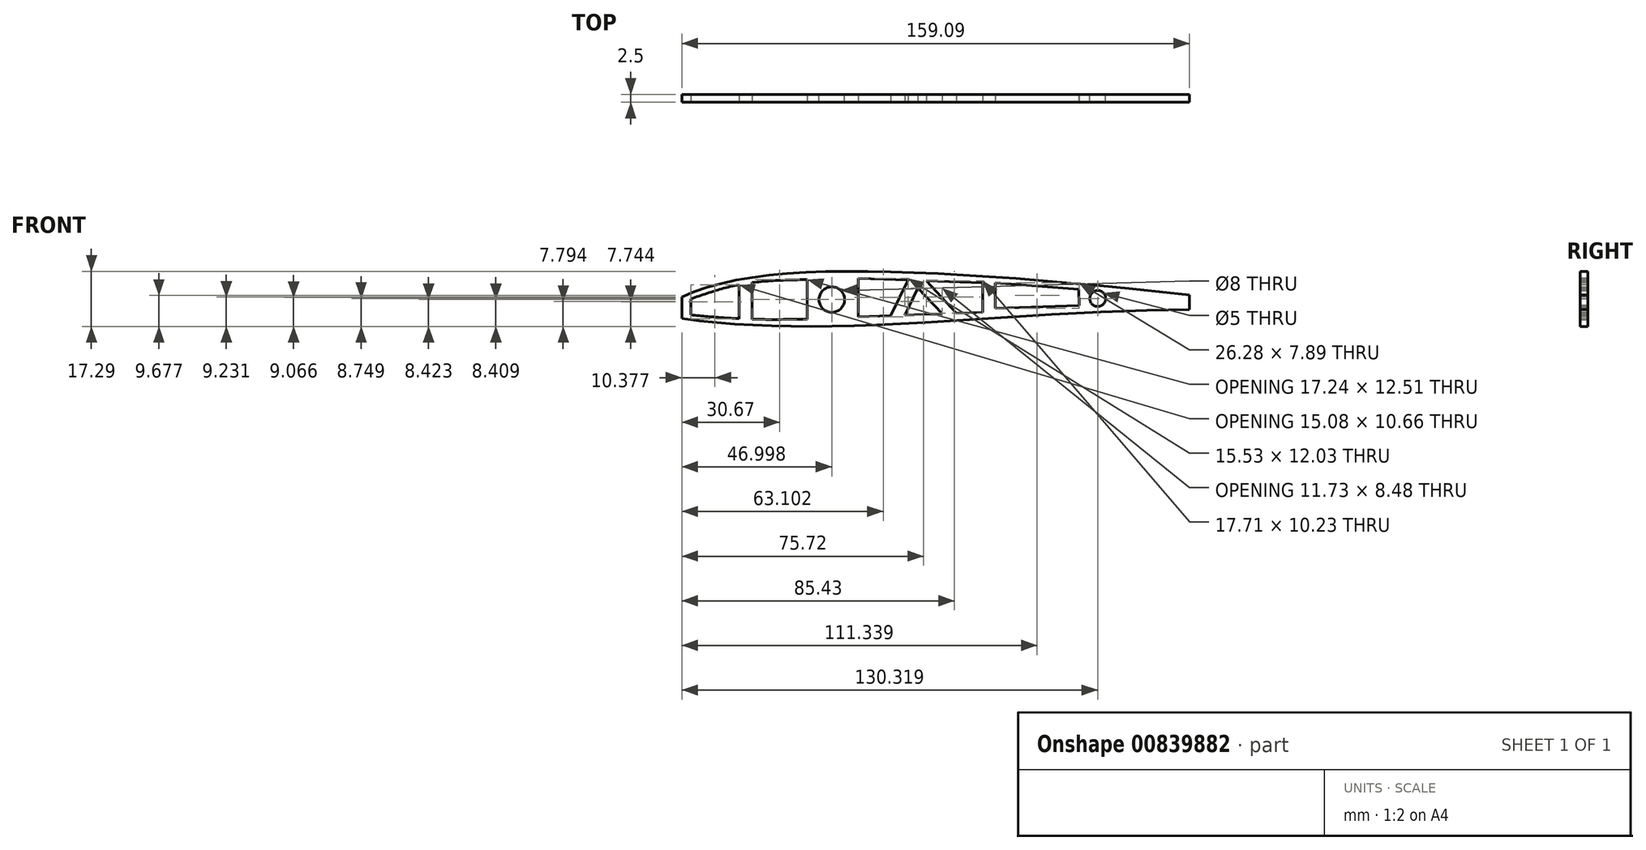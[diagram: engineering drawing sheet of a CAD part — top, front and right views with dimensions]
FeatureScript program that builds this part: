
annotation { "Feature Type Name" : "Feature", "Feature Type Description" : "" }
export const myFeature = defineFeature(function(context is Context, id is Id, definition is map)
    precondition{}
    {
        {
            var Q0;
            Q0=qCreatedBy(makeId("Front.planeOp"),FACE);
            var sketch = newSketch(context, id + "F0", { "sketchPlane" : qUnion([Q0])});
            skPoint(sketch, "E0.middle", {"position": v(0, 0) * mm});
            skLineSegment(sketch, "E1", {"start": v(-99.95, -4.05) * mm, "end": v(-99.64, -4.05) * mm});
            skFitSpline(sketch, "E2", {"points": [v(-96.98, -0.81) * mm, v(-45.24, 7.5) * mm, v(100, -4.05) * mm], "startDerivative": vector(97.58, 47.67) * mm, "endDerivative": vector(275.05, -31.29) * mm});
            skFitSpline(sketch, "E3", {"points": [v(-96.54, -7.34) * mm, v(-44.56, -9.6) * mm, v(41.7, -4.97) * mm, v(100, -4.05) * mm], "startDerivative": vector(159.07, -20.98) * mm, "endDerivative": vector(169.88, 6) * mm});
            skFitSpline(sketch, "E4", {"points": [v(-96.54, -7.34) * mm, v(-101.41, -5) * mm, v(-96.98, -0.81) * mm], "startDerivative": vector(-18.7, 3.9) * mm, "endDerivative": vector(17.62, 9.13) * mm});
            skArc(sketch, "E5.trimOffspring", {"start": v(-97.54, -7.12) * mm, "mid": v(-97.05, -7.27) * mm, "end": v(-96.54, -7.34) * mm});
            skFitSpline(sketch, "E6", {"points": [v(-96.34, -1.64) * mm, v(-45.34, 6.27) * mm, v(86.1, -3.38) * mm], "startDerivative": vector(82.57, 38.4) * mm, "endDerivative": vector(239.73, -24.74) * mm});
            skFitSpline(sketch, "E7", {"points": [v(-97.38, -6.05) * mm, v(-44.49, -7.96) * mm, v(41.39, -3.9) * mm, v(86.1, -3.38) * mm], "startDerivative": vector(144.05, -26.77) * mm, "endDerivative": vector(139.27, -2.3) * mm});
            skFitSpline(sketch, "E8", {"points": [v(-97.38, -6.05) * mm, v(-99.95, -4.56) * mm, v(-96.34, -1.64) * mm], "startDerivative": vector(-8.62, 1.03) * mm, "endDerivative": vector(10.24, 4.38) * mm});
            skSolve(sketch);
        }
        {
            var Q0;
            Q0=qCreatedBy(makeId("Front.planeOp"),FACE);
            var sketch = newSketch(context, id + "F1", { "sketchPlane" : qUnion([Q0])});
            skLineSegment(sketch, "E9", {"start": v(-109.84, -5.04) * mm, "end": v(108.45, -3.99) * mm});
            skCircle(sketch, "E10", {"center": v(-49.54, -1.37) * mm, "radius": 4 * mm});
            skCircle(sketch, "E11", {"center": v(33.78, -1.03) * mm, "radius": 2.5 * mm});
            skSolve(sketch);
        }
        {
            var Q0;
            {var subQ0=sQuery(id+"F0.wireOp",EDGE,"E6");Q0=makeQuery(id+"F0.imprint","IMPRINT",FACE,{"disambiguationData":[TD([[makeQuery(id+"F0.imprint","IMPRINT",EDGE,{"derivedFrom":subQ0}),-1.0]])]});}
            var Q1;
            {var subQ1=sQuery(id+"F0.wireOp",EDGE,"E2");Q1=makeQuery(id+"F0.imprint","IMPRINT",FACE,{"disambiguationData":[TD([[makeQuery(id+"F0.imprint","IMPRINT",EDGE,{"derivedFrom":subQ1}),-1.0]])]});}
            var Q2;
            Q2=makeQuery(id+"F1.imprint","IMPRINT",FACE,{"disambiguationData":[TD([[makeQuery(id+"F1.imprint","IMPRINT",EDGE,{"derivedFrom":sQuery(id+"F1.wireOp",EDGE,"E11")}),1.0]])]});
            var Q3;
            {var subQ0=sQuery(id+"F1.wireOp",EDGE,"E10");var subQ1=sQuery(id+"F1.wireOp",EDGE,"E9");var subQ2=makeQuery(id+"F1.imprint","INTERSECT",VERTEX,{"disambiguationData":[OD(0.0)],"derivedFrom":[subQ1,subQ0]});Q3=makeQuery(id+"F1.imprint","IMPRINT",FACE,{"disambiguationData":[TD([[makeQuery(id+"F1.imprint","IMPRINT",EDGE,{"disambiguationData":[TD([[subQ2,-1.0]])],"derivedFrom":subQ1}),1.0]])]});}
            var Q4;
            {var subQ0=sQuery(id+"F1.wireOp",EDGE,"E10");var subQ1=sQuery(id+"F1.wireOp",EDGE,"E9");var subQ2=makeQuery(id+"F1.imprint","INTERSECT",VERTEX,{"disambiguationData":[OD(0.0)],"derivedFrom":[subQ1,subQ0]});Q4=makeQuery(id+"F1.imprint","IMPRINT",FACE,{"disambiguationData":[TD([[makeQuery(id+"F1.imprint","IMPRINT",EDGE,{"disambiguationData":[TD([[subQ2,-1.0]])],"derivedFrom":subQ1}),-1.0]])]});}
            var Q5;
            {var subQ0=sQuery(id+"F0.wireOp",EDGE,"E5.trimOffspring");Q5=makeQuery(id+"F0.imprint","IMPRINT",FACE,{"disambiguationData":[TD([[makeQuery(id+"F0.imprint","IMPRINT",EDGE,{"derivedFrom":subQ0}),1.0]])]});}
            extrude(context, id + "F2", {"entities" : qUnion([Q0, Q1, Q2, Q3, Q4, Q5]), "depth" : 2.5 * mm, "offsetDistance" : 25 * mm});
        }
        {
            var Q0;
            Q0=qSketchRegion(id+"F1",true);
            var Q1;
            Q1=sQuery(id+"F1.wireOp",EDGE,"E11");
            var Q2;
            Q2=sQuery(id+"F1.wireOp",EDGE,"E10");
            extrude(context, id + "F3", {"entities" : qUnion([Q0]), "operationType" : NewBodyOperationType.REMOVE, "surfaceEntities" : qUnion([Q1, Q2]), "depth" : 2.5 * mm, "offsetDistance" : 25 * mm});
        }
        {
            var Q0;
            Q0=makeQuery(id+"F2.opExtrude","CAP_FACE",FACE,{"disambiguationData":[OSD([sQuery(id+"F0.wireOp",EDGE,"E2"),sQuery(id+"F0.wireOp",EDGE,"E3"),sQuery(id+"F0.wireOp",EDGE,"E4"),sQuery(id+"F0.wireOp",EDGE,"E5.trimOffspring")])],"isStart":false});
            var sketch = newSketch(context, id + "F4", { "sketchPlane" : qUnion([Q0])});
            skLineSegment(sketch, "E12", {"start": v(-96.54, -0.6) * mm, "end": v(-96.54, -7.34) * mm});
            skPoint(sketch, "E13.end.orphan", {"position": v(-96.98, -7.34) * mm});
            skLineSegment(sketch, "E14", {"start": v(-57.25, 4.9) * mm, "end": v(-57.25, -7.48) * mm});
            skFitSpline(sketch, "E15", {"points": [v(-57.25, -7.48) * mm, v(-75.97, -7.48) * mm, v(-93.7, -6.2) * mm], "startDerivative": vector(-37.23, -0.66) * mm, "endDerivative": vector(-35.67, 3.25) * mm});
            skFitSpline(sketch, "E16", {"points": [v(-57.25, 4.9) * mm, v(-77.46, 3.51) * mm, v(-93.7, -1.14) * mm], "startDerivative": vector(-39.88, -0.8) * mm, "endDerivative": vector(-32.92, -11.45) * mm});
            skLineSegment(sketch, "E17", {"start": v(-93.7, -1.14) * mm, "end": v(-93.7, -6.2) * mm});
            skLineSegment(sketch, "E18", {"start": v(1.66, 3.84) * mm, "end": v(1.66, -4.05) * mm});
            skLineSegment(sketch, "E19", {"start": v(1.66, -4.05) * mm, "end": v(27.94, -3.21) * mm});
            skLineSegment(sketch, "E20", {"start": v(27.94, -3.21) * mm, "end": v(27.77, 1.91) * mm});
            skLineSegment(sketch, "E21", {"start": v(27.77, 1.91) * mm, "end": v(1.66, 3.84) * mm});
            skLineSegment(sketch, "E22", {"start": v(-78.62, 3.3) * mm, "end": v(-78.62, -7.37) * mm});
            skLineSegment(sketch, "E23", {"start": v(-74.49, 3.96) * mm, "end": v(-74.49, -7.53) * mm});
            skPoint(sketch, "E24.end.orphan", {"position": v(-41.2, -6.73) * mm});
            skLineSegment(sketch, "E25", {"start": v(62.55, 0.1) * mm, "end": v(62.55, -4.52) * mm});
            skLineSegment(sketch, "E26", {"start": v(-41.2, -6.73) * mm, "end": v(-41.2, 5.3) * mm});
            skLineSegment(sketch, "E27", {"start": v(-41.2, 5.3) * mm, "end": v(-2.26, 3.95) * mm});
            skPoint(sketch, "E28.end.orphan", {"position": v(-2.26, -4.05) * mm});
            skLineSegment(sketch, "E29", {"start": v(-2.26, 3.95) * mm, "end": v(-2.26, -5.37) * mm});
            skLineSegment(sketch, "E30", {"start": v(-2.26, -5.37) * mm, "end": v(-41.2, -6.73) * mm});
            skLineSegment(sketch, "E31", {"start": v(-31.14, -6.38) * mm, "end": v(-25.67, 4.76) * mm});
            skLineSegment(sketch, "E32", {"start": v(-19.96, 4.57) * mm, "end": v(-10.52, -5.66) * mm});
            skLineSegment(sketch, "E33", {"start": v(-22.52, 2.25) * mm, "end": v(-26.69, -6.23) * mm});
            skLineSegment(sketch, "E34", {"start": v(-22.52, 2.25) * mm, "end": v(-14.95, -5.82) * mm});
            skSolve(sketch);
        }
        {
            var Q0;
            {var subQ0=sQuery(id+"F4.wireOp",EDGE,"E12");Q0=makeQuery(id+"F4.imprint","IMPRINT",FACE,{"disambiguationData":[TD([[makeQuery(id+"F4.imprint","IMPRINT",EDGE,{"derivedFrom":subQ0}),-1.0]])]});}
            extrude(context, id + "F5", {"entities" : qUnion([Q0]), "operationType" : NewBodyOperationType.REMOVE, "oppositeDirection" : true, "depth" : 2.5 * mm, "offsetDistance" : 25 * mm});
        }
        {
            var Q0;
            Q0=makeQuery(id+"F4.imprint","IMPRINT",FACE,{"disambiguationData":[TD([[makeQuery(id+"F4.imprint","IMPRINT",EDGE,{"derivedFrom":sQuery(id+"F4.wireOp",EDGE,"E17")}),1.0]])]});
            var Q1;
            Q1=makeQuery(id+"F4.imprint","IMPRINT",FACE,{"disambiguationData":[TD([[makeQuery(id+"F4.imprint","IMPRINT",EDGE,{"derivedFrom":sQuery(id+"F4.wireOp",EDGE,"E14")}),-1.0]])]});
            var Q2;
            Q2=makeQuery(id+"F4.imprint","IMPRINT",FACE,{"disambiguationData":[TD([[makeQuery(id+"F4.imprint","IMPRINT",EDGE,{"derivedFrom":sQuery(id+"F4.wireOp",EDGE,"ihOaFOc2-DZBp-csgD-MqmE-PSnDPwuukMZ8.bottom")}),-1.0]])]});
            var Q3;
            Q3=makeQuery(id+"F4.imprint","IMPRINT",FACE,{"disambiguationData":[TD([[makeQuery(id+"F4.imprint","IMPRINT",EDGE,{"derivedFrom":sQuery(id+"F4.wireOp",EDGE,"E18")}),1.0]])]});
            extrude(context, id + "F6", {"entities" : qUnion([Q0, Q1, Q2, Q3]), "operationType" : NewBodyOperationType.REMOVE, "oppositeDirection" : true, "depth" : 2.5 * mm, "offsetDistance" : 25 * mm});
        }
        {
            var Q0;
            {var subQ0=sQuery(id+"F4.wireOp",EDGE,"E25");Q0=makeQuery(id+"F4.imprint","IMPRINT",FACE,{"disambiguationData":[TD([[makeQuery(id+"F4.imprint","IMPRINT",EDGE,{"derivedFrom":subQ0}),1.0]])]});}
            extrude(context, id + "F7", {"entities" : qUnion([Q0]), "operationType" : NewBodyOperationType.REMOVE, "oppositeDirection" : true, "depth" : 2.5 * mm, "offsetDistance" : 25 * mm});
        }
        {
            var Q0;
            Q0=makeQuery(id+"F4.imprint","IMPRINT",FACE,{"disambiguationData":[TD([[makeQuery(id+"F4.imprint","IMPRINT",EDGE,{"derivedFrom":sQuery(id+"F4.wireOp",EDGE,"E17")}),1.0]])]});
            var Q1;
            Q1=makeQuery(id+"F4.imprint","IMPRINT",FACE,{"disambiguationData":[TD([[makeQuery(id+"F4.imprint","IMPRINT",EDGE,{"derivedFrom":sQuery(id+"F4.wireOp",EDGE,"E14")}),-1.0]])]});
            var Q2;
            Q2=makeQuery(id+"F4.imprint","IMPRINT",FACE,{"disambiguationData":[TD([[makeQuery(id+"F4.imprint","IMPRINT",EDGE,{"derivedFrom":sQuery(id+"F4.wireOp",EDGE,"E26")}),-1.0]])]});
            var Q3;
            Q3=makeQuery(id+"F4.imprint","IMPRINT",FACE,{"disambiguationData":[TD([[makeQuery(id+"F4.imprint","IMPRINT",EDGE,{"derivedFrom":sQuery(id+"F4.wireOp",EDGE,"E18")}),1.0]])]});
            extrude(context, id + "F8", {"entities" : qUnion([Q0, Q1, Q2, Q3]), "operationType" : NewBodyOperationType.REMOVE, "oppositeDirection" : true, "depth" : 2.5 * mm, "offsetDistance" : 25 * mm});
        }
        {
            var Q0;
            {var subQ0=sQuery(id+"F4.wireOp",EDGE,"E33");Q0=makeQuery(id+"F4.imprint","IMPRINT",FACE,{"disambiguationData":[TD([[makeQuery(id+"F4.imprint","IMPRINT",EDGE,{"derivedFrom":subQ0}),1.0]])]});}
            var Q1;
            {var subQ0=sQuery(id+"F4.wireOp",EDGE,"E29");Q1=makeQuery(id+"F4.imprint","IMPRINT",FACE,{"disambiguationData":[TD([[makeQuery(id+"F4.imprint","IMPRINT",EDGE,{"derivedFrom":subQ0}),-1.0]])]});}
            var Q2;
            Q2=makeQuery(id+"F4.imprint","IMPRINT",FACE,{"disambiguationData":[TD([[makeQuery(id+"F4.imprint","IMPRINT",EDGE,{"derivedFrom":sQuery(id+"F4.wireOp",EDGE,"E18")}),1.0]])]});
            var Q3;
            Q3=makeQuery(id+"F4.imprint","IMPRINT",FACE,{"disambiguationData":[TD([[makeQuery(id+"F4.imprint","IMPRINT",EDGE,{"derivedFrom":sQuery(id+"F4.wireOp",EDGE,"E14")}),-1.0]])]});
            var Q4;
            Q4=makeQuery(id+"F4.imprint","IMPRINT",FACE,{"disambiguationData":[TD([[makeQuery(id+"F4.imprint","IMPRINT",EDGE,{"derivedFrom":sQuery(id+"F4.wireOp",EDGE,"E17")}),1.0]])]});
            var Q5;
            {var subQ0=sQuery(id+"F4.wireOp",EDGE,"E26");Q5=makeQuery(id+"F4.imprint","IMPRINT",FACE,{"disambiguationData":[TD([[makeQuery(id+"F4.imprint","IMPRINT",EDGE,{"derivedFrom":subQ0}),-1.0]])]});}
            extrude(context, id + "F9", {"entities" : qUnion([Q0, Q1, Q2, Q3, Q4, Q5]), "operationType" : NewBodyOperationType.REMOVE, "oppositeDirection" : true, "depth" : 2.5 * mm, "offsetDistance" : 25 * mm});
        }
    });
